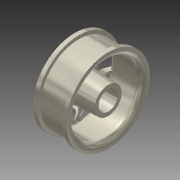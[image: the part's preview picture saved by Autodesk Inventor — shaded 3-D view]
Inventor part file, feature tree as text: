
AUTODESK INVENTOR PART (.ipt)
format: ipt  version: 2015 (Build 190159000, 159)  size: 900,608 bytes
history: native  units: in
note: dims shown in document units (in); Inventor stores cm internally (conversion verified against a paired STEP export)
features: revolve x5, sketch x3, other x3, plane x2, surface_op x1, shell x1, hole x1, fillet x1, pattern_circular x1, draft x1, extrude x1
ambient origin geometry x8: Origin, YZ Plane, XZ Plane, XY Plane, X Axis, Y Axis, Z Axis, Center Point
bodies: Solid1 (feature_tree)
feature tree (20):
  sketch  "Sketch1"  dims[d1=1.45in d2=0.07in]
  plane  "Work Plane1"
  surface_op  "Sculpt2"
  shell  "Shell1"  Thickness=0.58in
  revolve  "Revolution2"  [1 undecoded]
  revolve  "Revolution4"  [1 undecoded]
  revolve  "Revolution3"  [1 undecoded]
  plane  "Work Plane2"
  hole  "Hole1"  [1 undecoded]
  fillet  "Fillet2"  Radius=0.13in
  pattern_circular  "Circular Pattern1"  [2 undecoded]
  draft  "FaceDraft2"
  other  "Srf1"
  sketch  "Sketch2"  dims[d3=0.06in d7=0.33in]
  other  "Srf5"
  other  "Srf6"
  sketch  "Sketch3"  dims[d14=0.4947in d15=0.05in d16=0.2in d17=0.13in d19=0.6in d20=1.35in d21=0.2474in d22=0.2474in d24=0.3in d25=0.25in d27=-0.1in d31=0.1in d32=0.08in d33=1.35in d34=0.1in d35=0.4947in d36=0.375in d37=0.0in d38=0.01in d39=0.04in d41=0.4947in d42=0.47in d43=0.4947in d44=0.3in d45=0.75in d46=0.33in d47=0.17in d48=0.5635in d49=1.0in d50=0.8108in d51=1.9685in d52=360.0deg d54=0.0206in d55=0.4947in]
  revolve  "RevolutionSrf1"  [1 undecoded]
  revolve  "RevolutionSrf2"  [1 undecoded]
  extrude  "ExtrusionSrf2"  Depth=0.1in
note: 8 required parameter values undecoded (feature->parameter linkage not recoverable at this tier; creation-order binding heuristic only, values carry confidence <= 0.55)